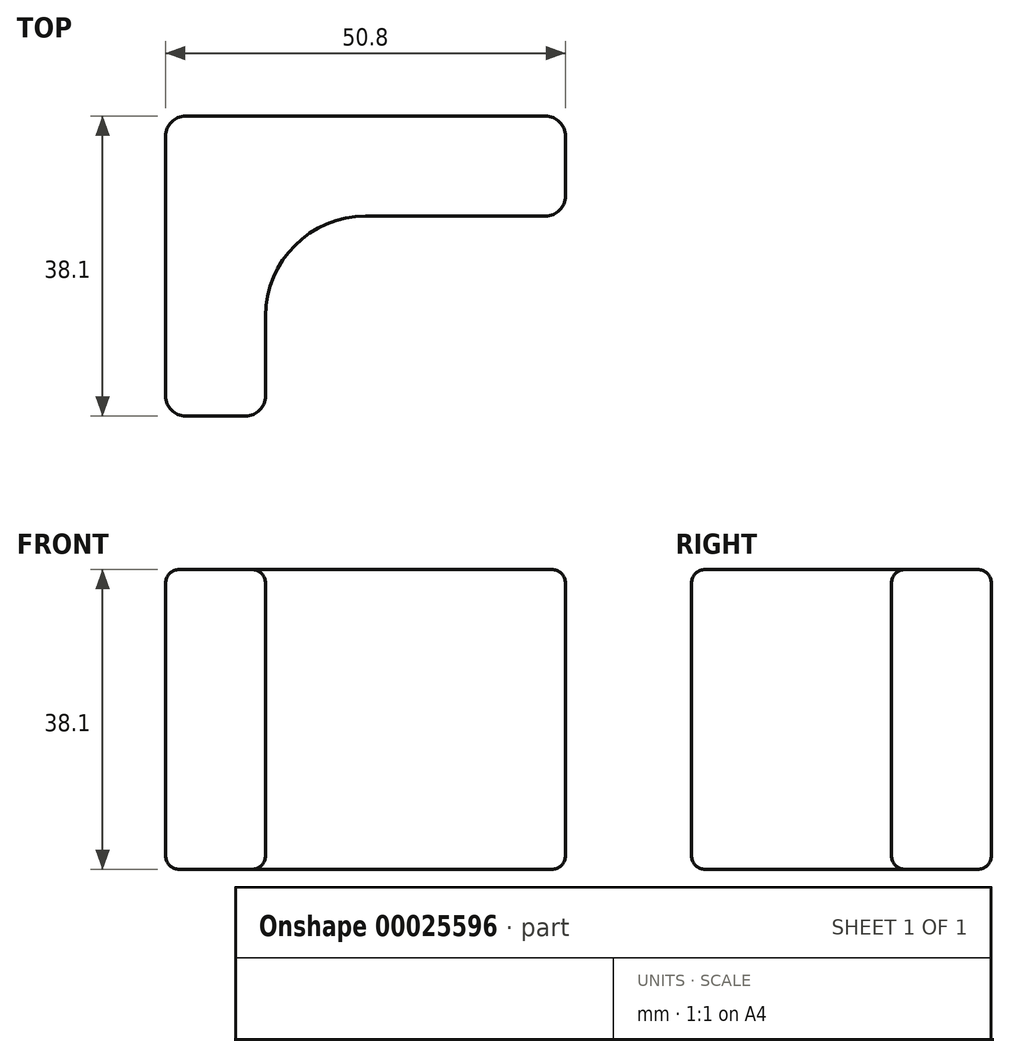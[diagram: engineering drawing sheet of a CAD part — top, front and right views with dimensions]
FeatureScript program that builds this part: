
annotation { "Feature Type Name" : "Feature", "Feature Type Description" : "" }
export const myFeature = defineFeature(function(context is Context, id is Id, definition is map)
    precondition{}
    {
        {
            var Q0;
            Q0=qCreatedBy(makeId("Top.planeOp"),FACE);
            var sketch = newSketch(context, id + "F0", { "sketchPlane" : qUnion([Q0])});
            skLineSegment(sketch, "E0", {"start": v(0, 0) * mm, "end": v(0, 38.1) * mm});
            skLineSegment(sketch, "E1", {"start": v(0, 38.1) * mm, "end": v(50.8, 38.1) * mm});
            skLineSegment(sketch, "E2", {"start": v(50.8, 38.1) * mm, "end": v(50.8, 25.4) * mm});
            skLineSegment(sketch, "E3", {"start": v(50.8, 25.4) * mm, "end": v(12.7, 25.4) * mm});
            skLineSegment(sketch, "E4", {"start": v(12.7, 25.4) * mm, "end": v(12.7, 0) * mm});
            skLineSegment(sketch, "E5", {"start": v(12.7, 0) * mm, "end": v(0, 0) * mm});
            skSolve(sketch);
        }
        {
            var Q0;
            Q0 = qSketchRegion(id + "F0", true);
            extrude(context, id + "F1", {"entities" : qUnion([Q0]), "depth" : 38.1 * mm});
        }
        {
            var Q0;
            Q0=makeQuery(id+"F1.opExtrude","SWEPT_EDGE",EDGE,{"disambiguationData":[OSD([sQuery(id+"F0.wireOp",EDGE,"E3"),sQuery(id+"F0.wireOp",EDGE,"E4")])]});
            fillet(context, id + "F2", {"entities" : qUnion([Q0]), "radius" : 12.7 * mm, "tangentPropagation" : true, "allowEdgeOverflow" : false});
        }
        {
            var Q0;
            Q0=makeQuery(id+"F1.opExtrude","SWEPT_EDGE",EDGE,{"disambiguationData":[OSD([sQuery(id+"F0.wireOp",EDGE,"E4"),sQuery(id+"F0.wireOp",EDGE,"E5")])]});
            var Q1;
            Q1=makeQuery(id+"F1.opExtrude","SWEPT_EDGE",EDGE,{"disambiguationData":[OSD([sQuery(id+"F0.wireOp",EDGE,"E0"),sQuery(id+"F0.wireOp",EDGE,"E5")])]});
            var Q2;
            Q2=makeQuery(id+"F1.opExtrude","SWEPT_EDGE",EDGE,{"disambiguationData":[OSD([sQuery(id+"F0.wireOp",EDGE,"E2"),sQuery(id+"F0.wireOp",EDGE,"E3")])]});
            var Q3;
            Q3=makeQuery(id+"F1.opExtrude","SWEPT_EDGE",EDGE,{"disambiguationData":[OSD([sQuery(id+"F0.wireOp",EDGE,"E1"),sQuery(id+"F0.wireOp",EDGE,"E2")])]});
            var Q4;
            Q4=makeQuery(id+"F1.opExtrude","SWEPT_EDGE",EDGE,{"disambiguationData":[OSD([sQuery(id+"F0.wireOp",EDGE,"E0"),sQuery(id+"F0.wireOp",EDGE,"E1")])]});
            fillet(context, id + "F3", {"entities" : qUnion([Q0, Q1, Q2, Q3, Q4]), "radius" : 2.54 * mm, "tangentPropagation" : true, "allowEdgeOverflow" : false});
        }
        {
            var Q0;
            Q0=makeQuery(id+"F1.opExtrude","CAP_EDGE",EDGE,{"disambiguationData":[OSD([sQuery(id+"F0.wireOp",EDGE,"E1")])],"isStart":false});
            var Q1;
            Q1=makeQuery(id+"F1.opExtrude","CAP_EDGE",EDGE,{"disambiguationData":[OSD([sQuery(id+"F0.wireOp",EDGE,"E1")])],"isStart":true});
            fillet(context, id + "F4", {"entities" : qUnion([Q0, Q1]), "radius" : 1.78 * mm, "tangentPropagation" : true, "allowEdgeOverflow" : false});
        }
    });
